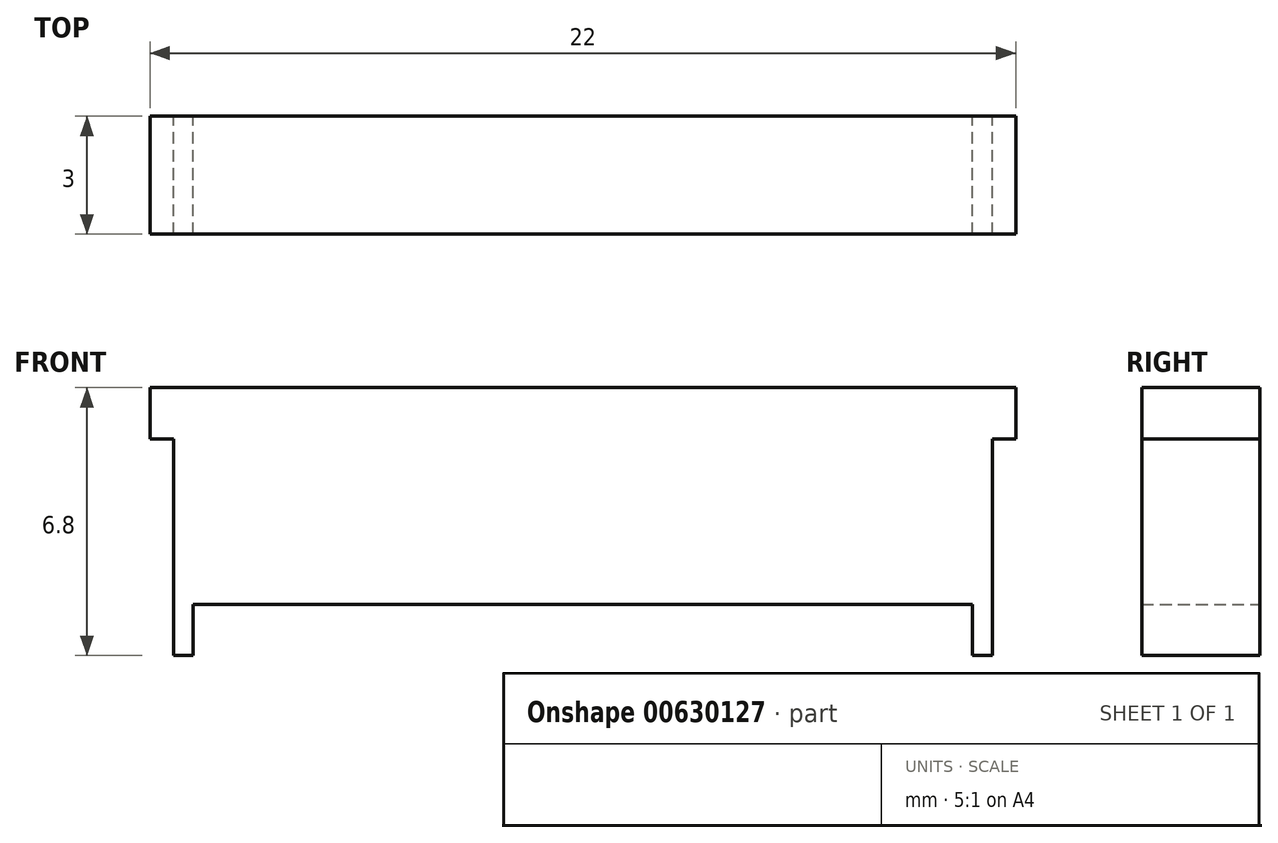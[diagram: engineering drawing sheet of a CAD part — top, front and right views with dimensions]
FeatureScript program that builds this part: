
annotation { "Feature Type Name" : "Feature", "Feature Type Description" : "" }
export const myFeature = defineFeature(function(context is Context, id is Id, definition is map)
    precondition{}
    {
        {
            var Q0;
            Q0=qCreatedBy(makeId("Front.planeOp"),FACE);
            var sketch = newSketch(context, id + "F0", { "sketchPlane" : qUnion([Q0])});
            skLineSegment(sketch, "E0.bottom", {"start": v(0.5, 0) * mm, "end": v(20.3, 0) * mm});
            skLineSegment(sketch, "E0.left", {"start": v(0, 0) * mm, "end": v(0, 4.2) * mm});
            skLineSegment(sketch, "E0.right", {"start": v(20.8, 0) * mm, "end": v(20.8, 4.2) * mm});
            skLineSegment(sketch, "E1.bottom", {"start": v(-0.6, 4.2) * mm, "end": v(0, 4.2) * mm});
            skLineSegment(sketch, "E1.top", {"start": v(-0.6, 5.5) * mm, "end": v(21.4, 5.5) * mm});
            skLineSegment(sketch, "E1.left", {"start": v(-0.6, 4.2) * mm, "end": v(-0.6, 5.5) * mm});
            skLineSegment(sketch, "E1.right", {"start": v(21.4, 4.2) * mm, "end": v(21.4, 5.5) * mm});
            skLineSegment(sketch, "E2.trimOffspring", {"start": v(20.8, 4.2) * mm, "end": v(21.4, 4.2) * mm});
            skLineSegment(sketch, "E3", {"start": v(0, 0) * mm, "end": v(0, -1.3) * mm});
            skLineSegment(sketch, "E4", {"start": v(0, -1.3) * mm, "end": v(0.5, -1.3) * mm});
            skLineSegment(sketch, "E5", {"start": v(0.5, -1.3) * mm, "end": v(0.5, 0) * mm});
            skLineSegment(sketch, "E6", {"start": v(20.8, 0) * mm, "end": v(20.8, -1.3) * mm});
            skLineSegment(sketch, "E7", {"start": v(20.8, -1.3) * mm, "end": v(20.3, -1.3) * mm});
            skLineSegment(sketch, "E8", {"start": v(20.3, -1.3) * mm, "end": v(20.3, 0) * mm});
            skSolve(sketch);
        }
        {
            var Q0;
            Q0=qSketchRegion(id+"F0",true);
            extrude(context, id + "F1", {"entities" : qUnion([Q0]), "depth" : 3 * mm});
        }
    });
